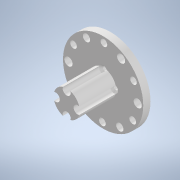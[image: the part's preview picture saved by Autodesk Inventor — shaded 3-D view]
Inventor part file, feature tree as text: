
AUTODESK INVENTOR PART (.ipt)
format: ipt  version: 2020 (Build 240168000, 168)  size: 246,272 bytes
history: native  units: mm
features: reference x12, other x5, extrude x4, sketch x4, fillet x1, hole x1
ambient origin geometry x8: Origin, YZ Plane, XZ Plane, XY Plane, X Axis, Y Axis, Z Axis, Center Point
bodies: Solid1 (feature_tree)
feature tree (27):
  extrude  "Extrusion1"  Depth=35.0mm TaperAngle=0.0deg
  extrude  "Extrusion2"  Depth=5.0mm TaperAngle=0.0deg
  fillet  "Fillet1"  Radius=5.0mm
  extrude  "Extrusion3"  Depth=10.0mm
  hole  "Hole2"  [1 undecoded]
  extrude  "Extrusion4"  [1 undecoded]
  sketch  "Sketch1"  dims[d0=35.0mm d1=2.0mm d2=0.0mm]
  sketch  "Sketch2"  dims[d3=55.0mm d4=5.0mm d5=0.0mm d6=5.0mm]
  sketch  "Sketch3"  dims[d7=10.0mm d8=0.0mm d9=17.9mm]
  reference  "Reference3"
  reference  "Reference4"
  reference  "Reference5"
  reference  "Reference6"
  reference  "Reference7"
  reference  "Reference8"
  reference  "Reference9"
  reference  "Reference10"
  reference  "Reference11"
  reference  "Reference12"
  reference  "Reference13"
  reference  "Reference14"
  sketch  "Sketch5"  dims[d12=15.0mm d20=2.9mm d21=6.0mm d22=5.5mm d23=2.0mm d24=90.0deg d25=20.0mm d26=0.0mm d27=35.0mm d28=0.0mm]
  other  "<userpath>\Desktop\KangKangBalancing\KangKang.iam"
  other  "KangKang.iam"
  other  "100mm-Plastic-Omni-Wheel:1"
  other  "A1_ASM_20"
  other  "F2_19"
note: 2 required parameter values undecoded (feature->parameter linkage not recoverable at this tier; creation-order binding heuristic only, values carry confidence <= 0.55)
